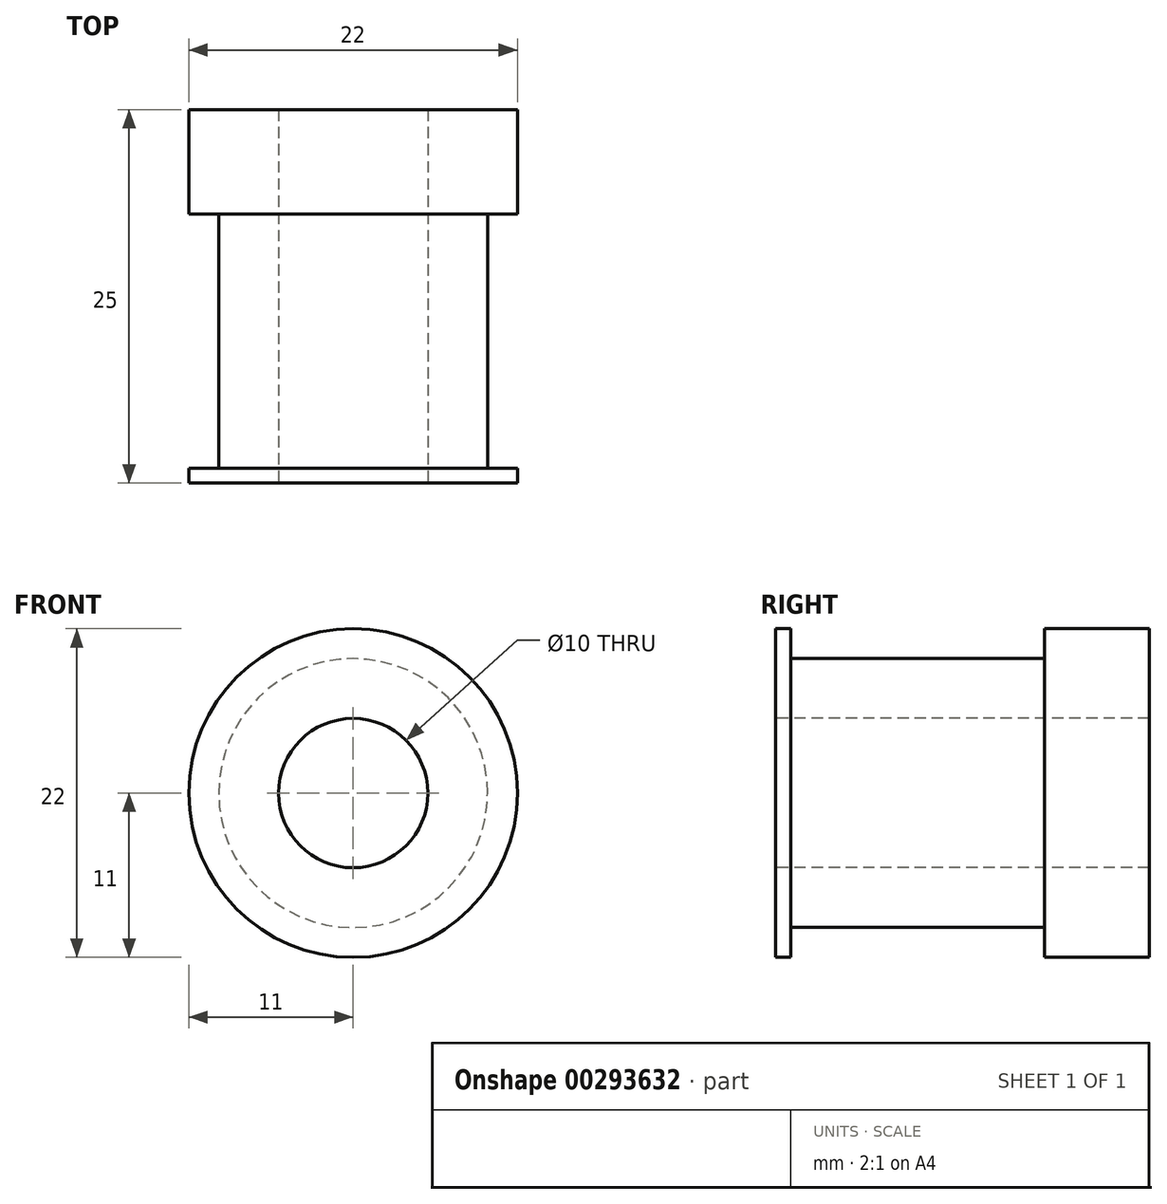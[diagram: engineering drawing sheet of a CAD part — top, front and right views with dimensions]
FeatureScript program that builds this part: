
annotation { "Feature Type Name" : "Feature", "Feature Type Description" : "" }
export const myFeature = defineFeature(function(context is Context, id is Id, definition is map)
    precondition{}
    {
        {
            var Q0;
            Q0=qCreatedBy(makeId("Front.planeOp"),FACE);
            var sketch = newSketch(context, id + "F0", { "sketchPlane" : qUnion([Q0])});
            skCircle(sketch, "E0", {"center": v(0, 0) * mm, "radius": 9 * mm});
            skSolve(sketch);
        }
        {
            var Q0;
            Q0 = qSketchRegion(id + "F0", true);
            extrude(context, id + "F1", {"entities" : qUnion([Q0]), "offsetDistance" : 25 * mm, "depth" : 9.5 * mm});
        }
        {
            var Q0;
            Q0=makeQuery(id+"F1.opExtrude","CAP_FACE",FACE,{"disambiguationData":[OSD([sQuery(id+"F0.wireOp",EDGE,"E0")])],"isStart":false});
            var sketch = newSketch(context, id + "F2", { "sketchPlane" : qUnion([Q0])});
            skCircle(sketch, "E1", {"center": v(0, 0) * mm, "radius": 11 * mm});
            skSolve(sketch);
        }
        {
            var Q0;
            Q0 = qSketchRegion(id + "F2", true);
            extrude(context, id + "F3", {"entities" : qUnion([Q0]), "operationType" : NewBodyOperationType.ADD, "oppositeDirection" : true, "depth" : 1 * mm});
        }
        {
            var Q0;
            Q0=makeQuery(id+"F1.opExtrude","SWEPT_BODY",BODY,{"disambiguationData":[OSD([sQuery(id+"F0.wireOp",EDGE,"E0")])]});
            var Q1;
            Q1=qCreatedBy(makeId("Front.planeOp"),FACE);
            mirror(context, id + "F4", {"operationType" : NewBodyOperationType.ADD, "entities" : qUnion([Q0]), "mirrorPlane" : qUnion([Q1])});
        }
        {
            var Q0;
            Q0=makeQuery(id+"F4.opPattern","COPY",FACE,{"derivedFrom":makeQuery(id+"F3.boolean.opBoolean","MERGE",FACE,{"derivedFrom":[makeQuery(id+"F1.opExtrude","CAP_FACE",FACE,{"disambiguationData":[OSD([sQuery(id+"F0.wireOp",EDGE,"E0")])],"isStart":false}),makeQuery(id+"F3.opExtrude","CAP_FACE",FACE,{"disambiguationData":[OSD([sQuery(id+"F2.wireOp",EDGE,"E1")])],"isStart":true})]}),"instanceName":"1"});
            extrude(context, id + "F5", {"entities" : qUnion([Q0]), "operationType" : NewBodyOperationType.ADD, "depth" : 6 * mm, "offsetDistance" : 25 * mm});
        }
        {
            var Q0;
            Q0=makeQuery(id+"F3.boolean.opBoolean","MERGE",FACE,{"derivedFrom":[makeQuery(id+"F1.opExtrude","CAP_FACE",FACE,{"disambiguationData":[OSD([sQuery(id+"F0.wireOp",EDGE,"E0")])],"isStart":false}),makeQuery(id+"F3.opExtrude","CAP_FACE",FACE,{"disambiguationData":[OSD([sQuery(id+"F2.wireOp",EDGE,"E1")])],"isStart":true})]});
            var sketch = newSketch(context, id + "F6", { "sketchPlane" : qUnion([Q0])});
            skPoint(sketch, "E2", {"position": v(0, 0) * mm});
            skCircle(sketch, "E3", {"center": v(0, 0) * mm, "radius": 5 * mm});
            skSolve(sketch);
        }
        {
            var Q0;
            Q0=makeQuery(id+"F6.imprint","IMPRINT",FACE,{"disambiguationData":[TD([[makeQuery(id+"F6.imprint","IMPRINT",EDGE,{"derivedFrom":sQuery(id+"F6.wireOp",EDGE,"E3")}),1.0]])]});
            extrude(context, id + "F7", {"entities" : qUnion([Q0]), "operationType" : NewBodyOperationType.REMOVE, "oppositeDirection" : true, "depth" : 25 * mm, "offsetDistance" : 25 * mm});
        }
    });
